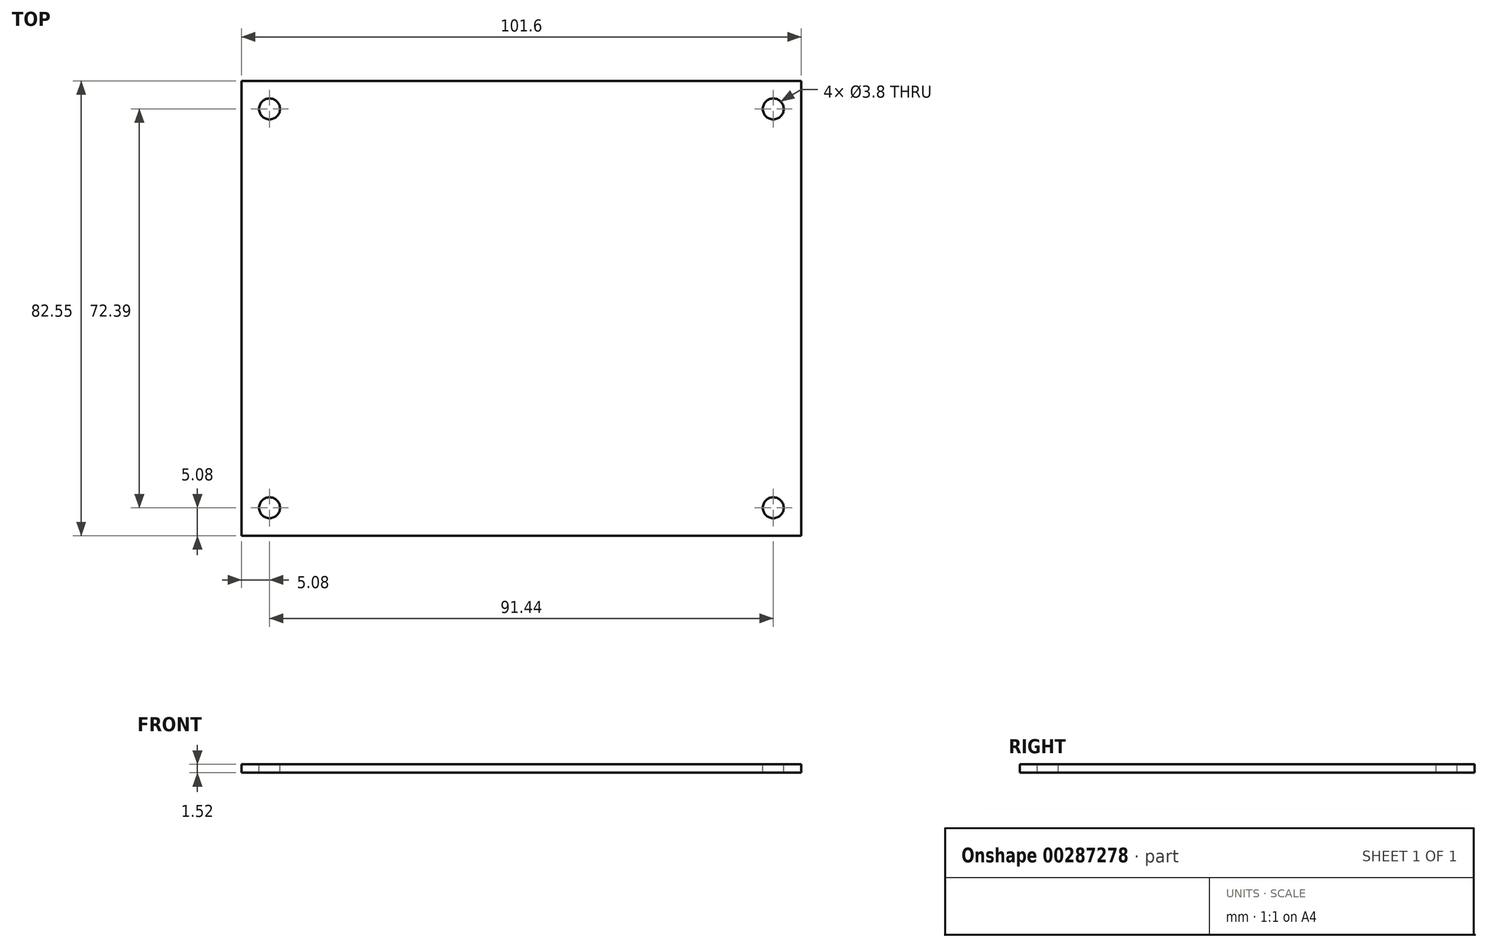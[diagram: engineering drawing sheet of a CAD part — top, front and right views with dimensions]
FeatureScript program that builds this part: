
annotation { "Feature Type Name" : "Feature", "Feature Type Description" : "" }
export const myFeature = defineFeature(function(context is Context, id is Id, definition is map)
    precondition{}
    {
        {
            var Q0;
            Q0=qCreatedBy(makeId("Top.planeOp"),FACE);
            var sketch = newSketch(context, id + "F0", { "sketchPlane" : qUnion([Q0])});
            skLineSegment(sketch, "E0.bottom", {"start": v(0, 0) * mm, "end": v(101.6, 0) * mm});
            skLineSegment(sketch, "E0.top", {"start": v(0, 82.55) * mm, "end": v(101.6, 82.55) * mm});
            skLineSegment(sketch, "E0.left", {"start": v(0, 0) * mm, "end": v(0, 82.55) * mm});
            skLineSegment(sketch, "E0.right", {"start": v(101.6, 0) * mm, "end": v(101.6, 82.55) * mm});
            skSolve(sketch);
        }
        {
            var Q0;
            Q0 = qSketchRegion(id + "F0", true);
            extrude(context, id + "F1", {"entities" : qUnion([Q0]), "depth" : 1.52 * mm});
        }
        {
            var Q0;
            Q0=makeQuery(id+"F1.opExtrude","CAP_FACE",FACE,{"disambiguationData":[OSD([sQuery(id+"F0.wireOp",EDGE,"E0.bottom"),sQuery(id+"F0.wireOp",EDGE,"E0.top"),sQuery(id+"F0.wireOp",EDGE,"E0.left"),sQuery(id+"F0.wireOp",EDGE,"E0.right")])],"isStart":false});
            var sketch = newSketch(context, id + "F2", { "sketchPlane" : qUnion([Q0])});
            skPoint(sketch, "E1", {"position": v(5.08, 77.47) * mm});
            skPoint(sketch, "E2", {"position": v(96.52, 77.47) * mm});
            skPoint(sketch, "E3", {"position": v(96.52, 5.08) * mm});
            skPoint(sketch, "E4", {"position": v(5.08, 5.08) * mm});
            skSolve(sketch);
        }
        {
            var Q0;
            Q0=sQuery(id+"F2.wireOp",VERTEX,"E1");
            var Q1;
            Q1=sQuery(id+"F2.wireOp",VERTEX,"E2");
            var Q2;
            Q2=sQuery(id+"F2.wireOp",VERTEX,"E4");
            var Q3;
            Q3=sQuery(id+"F2.wireOp",VERTEX,"E3");
            var Q4;
            Q4=makeQuery(id+"F1.opExtrude","SWEPT_BODY",BODY,{"disambiguationData":[OSD([sQuery(id+"F0.wireOp",EDGE,"E0.bottom"),sQuery(id+"F0.wireOp",EDGE,"E0.top"),sQuery(id+"F0.wireOp",EDGE,"E0.left"),sQuery(id+"F0.wireOp",EDGE,"E0.right")])]});
            hole(context, id + "F3", {"style" : HoleStyle.SIMPLE, "endStyle" : HoleEndStyle.THROUGH, "standardTappedOrClearance" : lookupTablePath({ "standard" : "ANSI", "fit" : "Normal (ASME)", "size" : "#6", "type" : "Clearance" }), "standardBlindInLast" : lookupTablePath({ "fit" : "Free", "standard" : "ANSI", "size" : "#6", "type" : "Clearance" }), "holeDiameter" : 3.8 * mm, "isTappedThrough" : true, "tappedDepth" : 2.4 * mm, "tapClearance" : 3, "startFromSketch" : true, "locations" : qUnion([Q0, Q1, Q2, Q3]), "scope" : qUnion([Q4])});
        }
    });
